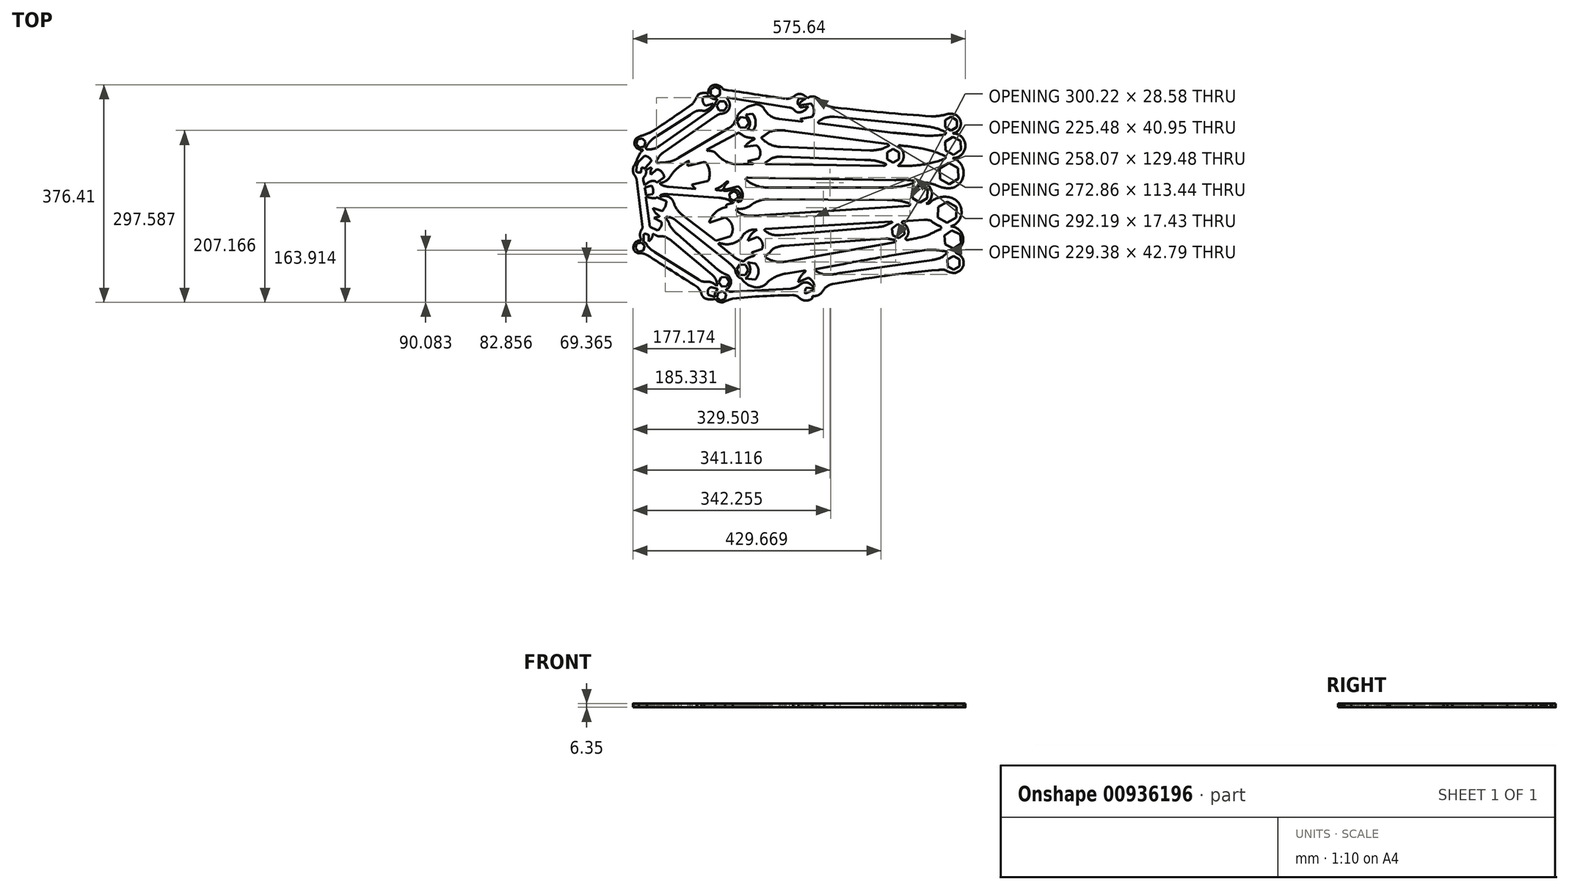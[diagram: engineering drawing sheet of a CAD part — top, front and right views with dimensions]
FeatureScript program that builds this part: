
annotation { "Feature Type Name" : "Feature", "Feature Type Description" : "" }
export const myFeature = defineFeature(function(context is Context, id is Id, definition is map)
    precondition{}
    {
        {
            var Q0;
            Q0=qCreatedBy(makeId("Top.planeOp"),FACE);
            var sketch = newSketch(context, id + "F0", { "sketchPlane" : qUnion([Q0])});
            skArc(sketch, "E0", {"start": v(-55.05, 260.44) * mm, "mid": v(-35.77, 286.45) * mm, "end": v(-55.34, 312.24) * mm});
            skArc(sketch, "E1", {"start": v(-55.34, 312.24) * mm, "mid": v(-32.71, 333.5) * mm, "end": v(-55.34, 354.78) * mm});
            skArc(sketch, "E2", {"start": v(-55.34, 354.78) * mm, "mid": v(-40.48, 371.7) * mm, "end": v(-55.34, 388.63) * mm});
            skArc(sketch, "E3", {"start": v(-58.23, 193.89) * mm, "mid": v(-39.5, 221.81) * mm, "end": v(-64.02, 244.82) * mm});
            skArc(sketch, "E4", {"start": v(-48.1, 151.93) * mm, "mid": v(-37.16, 176.78) * mm, "end": v(-58.23, 193.89) * mm});
            skArc(sketch, "E5", {"start": v(-50.13, 113.44) * mm, "mid": v(-35.84, 129.58) * mm, "end": v(-48.1, 147.3) * mm});
            skArc(sketch, "E6", {"start": v(-48.1, 151.93) * mm, "mid": v(-49.62, 149.62) * mm, "end": v(-48.1, 147.3) * mm});
            skArc(sketch, "E7", {"start": v(-67.06, 118.5) * mm, "mid": v(-59.11, 114.24) * mm, "end": v(-50.13, 113.44) * mm});
            skArc(sketch, "E8", {"start": v(-67.06, 118.5) * mm, "mid": v(-73.43, 118.66) * mm, "end": v(-79.8, 118.5) * mm});
            skArc(sketch, "E9", {"start": v(-79.8, 118.5) * mm, "mid": v(-171.14, 108.32) * mm, "end": v(-261.94, 94.05) * mm});
            skArc(sketch, "E10", {"start": v(-261.94, 94.05) * mm, "mid": v(-270.5, 91.02) * mm, "end": v(-277.56, 85.32) * mm});
            skArc(sketch, "E11", {"start": v(-297.54, 73.15) * mm, "mid": v(-285.53, 75.93) * mm, "end": v(-277.56, 85.32) * mm});
            skArc(sketch, "E12", {"start": v(-321.56, 71.59) * mm, "mid": v(-310, 65.3) * mm, "end": v(-297.54, 69.56) * mm});
            skArc(sketch, "E13", {"start": v(-321.56, 71.59) * mm, "mid": v(-326.02, 73.88) * mm, "end": v(-330.96, 74.77) * mm});
            skArc(sketch, "E14", {"start": v(-330.96, 74.77) * mm, "mid": v(-383.12, 73.1) * mm, "end": v(-435.13, 68.84) * mm});
            skArc(sketch, "E15", {"start": v(-435.13, 68.84) * mm, "mid": v(-442.05, 66.61) * mm, "end": v(-448.79, 63.89) * mm});
            skArc(sketch, "E16", {"start": v(-465.74, 68.84) * mm, "mid": v(-458.25, 62.97) * mm, "end": v(-448.79, 63.89) * mm});
            skArc(sketch, "E17", {"start": v(-484.84, 70.12) * mm, "mid": v(-475.44, 67.23) * mm, "end": v(-465.74, 68.84) * mm});
            skArc(sketch, "E18", {"start": v(-489.9, 78.95) * mm, "mid": v(-488.33, 73.99) * mm, "end": v(-484.84, 70.12) * mm});
            skArc(sketch, "E19", {"start": v(-489.9, 78.95) * mm, "mid": v(-493.3, 84.37) * mm, "end": v(-497.34, 89.32) * mm});
            skArc(sketch, "E20", {"start": v(-583.93, 144.4) * mm, "mid": v(-540.7, 116.75) * mm, "end": v(-497.34, 89.32) * mm});
            skArc(sketch, "E21", {"start": v(-583.93, 144.4) * mm, "mid": v(-590.67, 146.93) * mm, "end": v(-597.87, 147.3) * mm});
            skArc(sketch, "E22", {"start": v(-606.71, 161.55) * mm, "mid": v(-606, 152.12) * mm, "end": v(-597.87, 147.3) * mm});
            skArc(sketch, "E23", {"start": v(-594.42, 169.3) * mm, "mid": v(-601.98, 167.67) * mm, "end": v(-606.71, 161.55) * mm});
            skArc(sketch, "E24", {"start": v(-593.23, 187.82) * mm, "mid": v(-595.96, 179.21) * mm, "end": v(-593.23, 170.6) * mm});
            skArc(sketch, "E25", {"start": v(-593.23, 187.82) * mm, "mid": v(-592.2, 189.97) * mm, "end": v(-591.78, 192.3) * mm});
            skArc(sketch, "E26", {"start": v(-591.78, 192.3) * mm, "mid": v(-596.7, 233.52) * mm, "end": v(-601.66, 274.73) * mm});
            skArc(sketch, "E27", {"start": v(-601.66, 274.73) * mm, "mid": v(-602.84, 277.85) * mm, "end": v(-604.25, 280.88) * mm});
            skArc(sketch, "E28", {"start": v(-604.25, 301.71) * mm, "mid": v(-608.35, 291.3) * mm, "end": v(-604.25, 280.88) * mm});
            skArc(sketch, "E29", {"start": v(-590.37, 326.53) * mm, "mid": v(-597.45, 317.75) * mm, "end": v(-601.66, 307.28) * mm});
            skArc(sketch, "E30", {"start": v(-604.25, 333.1) * mm, "mid": v(-598.39, 327.55) * mm, "end": v(-590.37, 326.53) * mm});
            skArc(sketch, "E31", {"start": v(-600.43, 347.65) * mm, "mid": v(-605.16, 341.12) * mm, "end": v(-604.25, 333.1) * mm});
            skArc(sketch, "E32", {"start": v(-591.78, 351.27) * mm, "mid": v(-596.23, 349.75) * mm, "end": v(-600.43, 347.65) * mm});
            skArc(sketch, "E33", {"start": v(-591.78, 351.27) * mm, "mid": v(-583.33, 354.16) * mm, "end": v(-575.25, 358) * mm});
            skArc(sketch, "E34", {"start": v(-575.25, 358) * mm, "mid": v(-540.45, 381.34) * mm, "end": v(-505.94, 405.1) * mm});
            skArc(sketch, "E35", {"start": v(-505.94, 405.1) * mm, "mid": v(-500.06, 413.35) * mm, "end": v(-495.19, 422.24) * mm});
            skArc(sketch, "E36", {"start": v(-477.33, 423.44) * mm, "mid": v(-486.4, 424.91) * mm, "end": v(-495.19, 422.24) * mm});
            skArc(sketch, "E37", {"start": v(-468.58, 438.6) * mm, "mid": v(-476.1, 432.83) * mm, "end": v(-477.33, 423.44) * mm});
            skArc(sketch, "E38", {"start": v(-453.3, 432.68) * mm, "mid": v(-460.1, 437.83) * mm, "end": v(-468.58, 438.6) * mm});
            skArc(sketch, "E39", {"start": v(-453.3, 432.68) * mm, "mid": v(-451.18, 431.1) * mm, "end": v(-448.68, 430.22) * mm});
            skArc(sketch, "E40", {"start": v(-448.68, 430.22) * mm, "mid": v(-395.94, 422.55) * mm, "end": v(-343.2, 414.89) * mm});
            skArc(sketch, "E41", {"start": v(-343.2, 414.89) * mm, "mid": v(-335.76, 415.8) * mm, "end": v(-329.02, 419.08) * mm});
            skArc(sketch, "E42", {"start": v(-314.84, 422.24) * mm, "mid": v(-322.42, 422.86) * mm, "end": v(-329.02, 419.08) * mm});
            skArc(sketch, "E43", {"start": v(-307.75, 417.2) * mm, "mid": v(-311.06, 420.06) * mm, "end": v(-314.84, 422.24) * mm});
            skArc(sketch, "E44", {"start": v(-290.54, 416.91) * mm, "mid": v(-298.22, 418.8) * mm, "end": v(-305.73, 416.33) * mm});
            skArc(sketch, "E45", {"start": v(-284.64, 413.56) * mm, "mid": v(-287.52, 415.36) * mm, "end": v(-290.54, 416.91) * mm});
            skArc(sketch, "E46", {"start": v(-284.64, 413.56) * mm, "mid": v(-280.96, 408.46) * mm, "end": v(-275.63, 405.1) * mm});
            skArc(sketch, "E47", {"start": v(-275.63, 405.1) * mm, "mid": v(-267.42, 401.3) * mm, "end": v(-258.53, 399.62) * mm});
            skArc(sketch, "E48", {"start": v(-258.53, 399.62) * mm, "mid": v(-175.22, 391.15) * mm, "end": v(-91.74, 384.4) * mm});
            skArc(sketch, "E49", {"start": v(-91.74, 384.4) * mm, "mid": v(-79.83, 385.04) * mm, "end": v(-68.09, 387.15) * mm});
            skArc(sketch, "E50", {"start": v(-55.34, 388.63) * mm, "mid": v(-61.8, 388.7) * mm, "end": v(-68.09, 387.15) * mm});
            skArc(sketch, "E51", {"start": v(-83.4, 265.2) * mm, "mid": v(-69.62, 260.51) * mm, "end": v(-55.05, 260.44) * mm});
            skArc(sketch, "E52", {"start": v(-83.4, 265.2) * mm, "mid": v(-92.57, 267.9) * mm, "end": v(-101.93, 269.83) * mm});
            skArc(sketch, "E53", {"start": v(-90.64, 251.46) * mm, "mid": v(-94.28, 261.88) * mm, "end": v(-101.93, 269.83) * mm});
            skArc(sketch, "E54", {"start": v(-100.48, 233.08) * mm, "mid": v(-93.22, 241.02) * mm, "end": v(-90.64, 251.46) * mm});
            skArc(sketch, "E55", {"start": v(-64.02, 244.82) * mm, "mid": v(-81.43, 242.82) * mm, "end": v(-96, 233.08) * mm});
            skLineSegment(sketch, "E56", {"start": v(-297.54, 69.56) * mm, "end": v(-297.54, 73.15) * mm});
            skLineSegment(sketch, "E57", {"start": v(-594.42, 169.3) * mm, "end": v(-593.23, 170.6) * mm});
            skLineSegment(sketch, "E58", {"start": v(-604.25, 301.71) * mm, "end": v(-601.66, 307.28) * mm});
            skLineSegment(sketch, "E59", {"start": v(-305.73, 416.33) * mm, "end": v(-307.75, 417.2) * mm});
            skCircle(sketch, "E60.cCircle", {"center": v(-57.55, 371.7) * mm, "radius": 10.32 * mm, "construction": true});
            skLineSegment(sketch, "E60.0", {"start": v(-57.68, 359.8) * mm, "end": v(-67.93, 365.86) * mm});
            skLineSegment(sketch, "E60.1", {"start": v(-67.93, 365.86) * mm, "end": v(-67.8, 377.77) * mm});
            skLineSegment(sketch, "E60.2", {"start": v(-67.8, 377.77) * mm, "end": v(-57.43, 383.62) * mm});
            skLineSegment(sketch, "E60.3", {"start": v(-57.43, 383.62) * mm, "end": v(-47.17, 377.55) * mm});
            skLineSegment(sketch, "E60.4", {"start": v(-47.17, 377.55) * mm, "end": v(-47.3, 365.64) * mm});
            skLineSegment(sketch, "E60.5", {"start": v(-47.3, 365.64) * mm, "end": v(-57.68, 359.8) * mm});
            skPoint(sketch, "E60.0.midPoint", {"position": v(-62.8, 362.82) * mm});
            skCircle(sketch, "E61.cCircle", {"center": v(-54.02, 333.5) * mm, "radius": 13.49 * mm, "construction": true});
            skLineSegment(sketch, "E61.0", {"start": v(-53.4, 317.95) * mm, "end": v(-67.18, 325.18) * mm});
            skLineSegment(sketch, "E61.1", {"start": v(-67.18, 325.18) * mm, "end": v(-67.81, 340.74) * mm});
            skLineSegment(sketch, "E61.2", {"start": v(-67.81, 340.74) * mm, "end": v(-54.65, 349.07) * mm});
            skLineSegment(sketch, "E61.3", {"start": v(-54.65, 349.07) * mm, "end": v(-40.86, 341.83) * mm});
            skLineSegment(sketch, "E61.4", {"start": v(-40.86, 341.83) * mm, "end": v(-40.23, 326.27) * mm});
            skLineSegment(sketch, "E61.5", {"start": v(-40.23, 326.27) * mm, "end": v(-53.4, 317.95) * mm});
            skPoint(sketch, "E61.0.midPoint", {"position": v(-60.29, 321.56) * mm});
            skCircle(sketch, "E62.cCircle", {"center": v(-61.13, 285.32) * mm, "radius": 15.88 * mm, "construction": true});
            skLineSegment(sketch, "E62.0", {"start": v(-61.01, 267) * mm, "end": v(-76.95, 276.05) * mm});
            skLineSegment(sketch, "E62.1", {"start": v(-76.95, 276.05) * mm, "end": v(-77.07, 294.38) * mm});
            skLineSegment(sketch, "E62.2", {"start": v(-77.07, 294.38) * mm, "end": v(-61.26, 303.65) * mm});
            skLineSegment(sketch, "E62.3", {"start": v(-61.26, 303.65) * mm, "end": v(-45.32, 294.6) * mm});
            skLineSegment(sketch, "E62.4", {"start": v(-45.32, 294.6) * mm, "end": v(-45.2, 276.26) * mm});
            skLineSegment(sketch, "E62.5", {"start": v(-45.2, 276.26) * mm, "end": v(-61.01, 267) * mm});
            skPoint(sketch, "E62.0.midPoint", {"position": v(-68.98, 271.52) * mm});
            skCircle(sketch, "E63.cCircle", {"center": v(-111.31, 250.03) * mm, "radius": 12.7 * mm, "construction": true});
            skLineSegment(sketch, "E63.0", {"start": v(-111.59, 235.37) * mm, "end": v(-124.15, 242.94) * mm});
            skLineSegment(sketch, "E63.1", {"start": v(-124.15, 242.94) * mm, "end": v(-123.87, 257.6) * mm});
            skLineSegment(sketch, "E63.2", {"start": v(-123.87, 257.6) * mm, "end": v(-111.03, 264.7) * mm});
            skLineSegment(sketch, "E63.3", {"start": v(-111.03, 264.7) * mm, "end": v(-98.47, 257.12) * mm});
            skLineSegment(sketch, "E63.4", {"start": v(-98.47, 257.12) * mm, "end": v(-98.75, 242.46) * mm});
            skLineSegment(sketch, "E63.5", {"start": v(-98.75, 242.46) * mm, "end": v(-111.59, 235.37) * mm});
            skPoint(sketch, "E63.0.midPoint", {"position": v(-117.87, 239.16) * mm});
            skCircle(sketch, "E64.cCircle", {"center": v(-64.33, 218.26) * mm, "radius": 15.88 * mm, "construction": true});
            skLineSegment(sketch, "E64.0", {"start": v(-64.51, 199.93) * mm, "end": v(-80.3, 209.26) * mm});
            skLineSegment(sketch, "E64.1", {"start": v(-80.3, 209.26) * mm, "end": v(-80.1, 227.59) * mm});
            skLineSegment(sketch, "E64.2", {"start": v(-80.1, 227.59) * mm, "end": v(-64.14, 236.6) * mm});
            skLineSegment(sketch, "E64.3", {"start": v(-64.14, 236.6) * mm, "end": v(-48.36, 227.27) * mm});
            skLineSegment(sketch, "E64.4", {"start": v(-48.36, 227.27) * mm, "end": v(-48.55, 208.94) * mm});
            skLineSegment(sketch, "E64.5", {"start": v(-48.55, 208.94) * mm, "end": v(-64.51, 199.93) * mm});
            skPoint(sketch, "E64.0.midPoint", {"position": v(-72.4, 204.6) * mm});
            skCircle(sketch, "E65.cCircle", {"center": v(-149.16, 185.48) * mm, "radius": 10.32 * mm, "construction": true});
            skLineSegment(sketch, "E65.0", {"start": v(-147.9, 173.63) * mm, "end": v(-158.79, 178.46) * mm});
            skLineSegment(sketch, "E65.1", {"start": v(-158.79, 178.46) * mm, "end": v(-160.05, 190.3) * mm});
            skLineSegment(sketch, "E65.2", {"start": v(-160.05, 190.3) * mm, "end": v(-150.42, 197.33) * mm});
            skLineSegment(sketch, "E65.3", {"start": v(-150.42, 197.33) * mm, "end": v(-139.53, 192.5) * mm});
            skLineSegment(sketch, "E65.4", {"start": v(-139.53, 192.5) * mm, "end": v(-138.27, 180.65) * mm});
            skLineSegment(sketch, "E65.5", {"start": v(-138.27, 180.65) * mm, "end": v(-147.9, 173.63) * mm});
            skPoint(sketch, "E65.0.midPoint", {"position": v(-153.34, 176.04) * mm});
            skCircle(sketch, "E66.cCircle", {"center": v(-54.8, 171.29) * mm, "radius": 13.49 * mm, "construction": true});
            skLineSegment(sketch, "E66.0", {"start": v(-53.58, 155.76) * mm, "end": v(-67.64, 162.47) * mm});
            skLineSegment(sketch, "E66.1", {"start": v(-67.64, 162.47) * mm, "end": v(-68.86, 178) * mm});
            skLineSegment(sketch, "E66.2", {"start": v(-68.86, 178) * mm, "end": v(-56.02, 186.81) * mm});
            skLineSegment(sketch, "E66.3", {"start": v(-56.02, 186.81) * mm, "end": v(-41.97, 180.11) * mm});
            skLineSegment(sketch, "E66.4", {"start": v(-41.97, 180.11) * mm, "end": v(-40.74, 164.58) * mm});
            skLineSegment(sketch, "E66.5", {"start": v(-40.74, 164.58) * mm, "end": v(-53.58, 155.76) * mm});
            skPoint(sketch, "E66.0.midPoint", {"position": v(-60.6, 159.11) * mm});
            skCircle(sketch, "E67.cCircle", {"center": v(-53.27, 130.62) * mm, "radius": 10.32 * mm, "construction": true});
            skLineSegment(sketch, "E67.0", {"start": v(-42.86, 124.82) * mm, "end": v(-53.1, 118.7) * mm});
            skLineSegment(sketch, "E67.1", {"start": v(-53.1, 118.7) * mm, "end": v(-63.5, 124.51) * mm});
            skLineSegment(sketch, "E67.2", {"start": v(-63.5, 124.51) * mm, "end": v(-63.67, 136.43) * mm});
            skLineSegment(sketch, "E67.3", {"start": v(-63.67, 136.43) * mm, "end": v(-53.44, 142.53) * mm});
            skLineSegment(sketch, "E67.4", {"start": v(-53.44, 142.53) * mm, "end": v(-43.04, 136.73) * mm});
            skLineSegment(sketch, "E67.5", {"start": v(-43.04, 136.73) * mm, "end": v(-42.86, 124.82) * mm});
            skPoint(sketch, "E67.0.midPoint", {"position": v(-47.98, 121.76) * mm});
            skCircle(sketch, "E68.cCircle", {"center": v(-157.91, 316.16) * mm, "radius": 10.32 * mm, "construction": true});
            skLineSegment(sketch, "E68.0", {"start": v(-168.23, 310.2) * mm, "end": v(-168.23, 322.12) * mm});
            skLineSegment(sketch, "E68.1", {"start": v(-168.23, 322.12) * mm, "end": v(-157.91, 328.08) * mm});
            skLineSegment(sketch, "E68.2", {"start": v(-157.91, 328.08) * mm, "end": v(-147.6, 322.12) * mm});
            skLineSegment(sketch, "E68.3", {"start": v(-147.6, 322.12) * mm, "end": v(-147.6, 310.2) * mm});
            skLineSegment(sketch, "E68.4", {"start": v(-147.6, 310.2) * mm, "end": v(-157.91, 304.25) * mm});
            skLineSegment(sketch, "E68.5", {"start": v(-157.91, 304.25) * mm, "end": v(-168.23, 310.2) * mm});
            skPoint(sketch, "E68.0.midPoint", {"position": v(-168.23, 316.16) * mm});
            skArc(sketch, "E69", {"start": v(-67.1, 356.86) * mm, "mid": v(-81.33, 363.08) * mm, "end": v(-96.49, 366.5) * mm});
            skArc(sketch, "E70", {"start": v(-117.16, 352.27) * mm, "mid": v(-92.55, 350.73) * mm, "end": v(-68, 353.19) * mm});
            skArc(sketch, "E71", {"start": v(-68.7, 315.98) * mm, "mid": v(-88.6, 323.76) * mm, "end": v(-109.35, 328.84) * mm});
            skArc(sketch, "E72", {"start": v(-111.65, 300.13) * mm, "mid": v(-89.98, 304.15) * mm, "end": v(-68.93, 310.7) * mm});
            skArc(sketch, "E73", {"start": v(-68, 353.19) * mm, "mid": v(-66.78, 354.83) * mm, "end": v(-67.1, 356.86) * mm});
            skArc(sketch, "E74", {"start": v(-68.93, 310.7) * mm, "mid": v(-66.96, 313.26) * mm, "end": v(-68.7, 315.98) * mm});
            skLineSegment(sketch, "E75", {"start": v(-96, 233.08) * mm, "end": v(-100.48, 233.08) * mm});
            skArc(sketch, "E76", {"start": v(-93.08, 204.03) * mm, "mid": v(-84.94, 198.29) * mm, "end": v(-76, 193.9) * mm});
            skArc(sketch, "E77", {"start": v(-93.08, 204.03) * mm, "mid": v(-98.82, 205.1) * mm, "end": v(-104.65, 205.33) * mm});
            skArc(sketch, "E78", {"start": v(-74.56, 189.7) * mm, "mid": v(-86.96, 183.92) * mm, "end": v(-99.15, 177.7) * mm});
            skArc(sketch, "E79", {"start": v(-134.17, 170.17) * mm, "mid": v(-116.6, 173.63) * mm, "end": v(-99.15, 177.7) * mm});
            skArc(sketch, "E80", {"start": v(-136.05, 173.2) * mm, "mid": v(-131.94, 188.07) * mm, "end": v(-142.56, 199.25) * mm});
            skLineSegment(sketch, "E81", {"start": v(-104.65, 205.33) * mm, "end": v(-141.4, 203.01) * mm});
            skArc(sketch, "E82", {"start": v(-141.4, 203.01) * mm, "mid": v(-142.3, 201.23) * mm, "end": v(-142.56, 199.25) * mm});
            skArc(sketch, "E83", {"start": v(-136.05, 173.2) * mm, "mid": v(-135.8, 171.26) * mm, "end": v(-134.17, 170.17) * mm});
            skArc(sketch, "E84", {"start": v(-74.56, 189.7) * mm, "mid": v(-74.67, 192.01) * mm, "end": v(-76, 193.9) * mm});
            skArc(sketch, "E85", {"start": v(-66, 150.5) * mm, "mid": v(-72.3, 151.46) * mm, "end": v(-78.62, 152.33) * mm});
            skArc(sketch, "E86", {"start": v(-78.62, 152.33) * mm, "mid": v(-89.14, 153.18) * mm, "end": v(-99.7, 152.96) * mm});
            skArc(sketch, "E87", {"start": v(-99.7, 152.96) * mm, "mid": v(-132, 148.18) * mm, "end": v(-164.2, 142.78) * mm});
            skArc(sketch, "E88", {"start": v(-164.2, 142.78) * mm, "mid": v(-202.8, 136.25) * mm, "end": v(-241.31, 129.29) * mm});
            skLineSegment(sketch, "E89", {"start": v(-241.31, 129.29) * mm, "end": v(-293.37, 119.57) * mm});
            skArc(sketch, "E90", {"start": v(-291.22, 116.51) * mm, "mid": v(-285, 113.2) * mm, "end": v(-278.35, 110.89) * mm});
            skArc(sketch, "E91", {"start": v(-278.35, 110.89) * mm, "mid": v(-264, 110.66) * mm, "end": v(-249.87, 113.18) * mm});
            skLineSegment(sketch, "E92", {"start": v(-249.87, 113.18) * mm, "end": v(-90.32, 135.62) * mm});
            skArc(sketch, "E93", {"start": v(-90.32, 135.62) * mm, "mid": v(-80.84, 137.71) * mm, "end": v(-71.8, 141.26) * mm});
            skArc(sketch, "E94", {"start": v(-64, 147.91) * mm, "mid": v(-68.09, 144.8) * mm, "end": v(-71.8, 141.26) * mm});
            skArc(sketch, "E95", {"start": v(-64, 147.91) * mm, "mid": v(-64.5, 149.58) * mm, "end": v(-66, 150.5) * mm});
            skArc(sketch, "E96", {"start": v(-293.37, 119.57) * mm, "mid": v(-292.66, 117.78) * mm, "end": v(-291.22, 116.51) * mm});
            skArc(sketch, "E97", {"start": v(-148.24, 298.5) * mm, "mid": v(-129.91, 298.62) * mm, "end": v(-111.65, 300.13) * mm});
            skArc(sketch, "E98", {"start": v(-148.59, 300.13) * mm, "mid": v(-139.57, 315.6) * mm, "end": v(-147.9, 331.45) * mm});
            skArc(sketch, "E99", {"start": v(-109.35, 328.84) * mm, "mid": v(-128.57, 331.94) * mm, "end": v(-147.9, 334.2) * mm});
            skArc(sketch, "E100", {"start": v(-147.9, 334.2) * mm, "mid": v(-148.37, 332.83) * mm, "end": v(-147.9, 331.45) * mm});
            skArc(sketch, "E101", {"start": v(-148.59, 300.13) * mm, "mid": v(-149.15, 299.16) * mm, "end": v(-148.24, 298.5) * mm});
            skArc(sketch, "E102", {"start": v(-96.49, 366.5) * mm, "mid": v(-111.46, 368.54) * mm, "end": v(-126.48, 370.2) * mm});
            skArc(sketch, "E103", {"start": v(-117.16, 352.27) * mm, "mid": v(-137.44, 354.16) * mm, "end": v(-157.73, 356.01) * mm});
            skArc(sketch, "E104", {"start": v(-259.78, 383.5) * mm, "mid": v(-274.29, 382.2) * mm, "end": v(-287.12, 375.3) * mm});
            skLineSegment(sketch, "E105", {"start": v(-259.78, 383.5) * mm, "end": v(-126.48, 370.2) * mm});
            skLineSegment(sketch, "E106", {"start": v(-157.73, 356.01) * mm, "end": v(-285.48, 372.02) * mm});
            skArc(sketch, "E107", {"start": v(-287.12, 375.3) * mm, "mid": v(-287.18, 373.22) * mm, "end": v(-285.48, 372.02) * mm});
            skArc(sketch, "E108", {"start": v(-164.93, 333.3) * mm, "mid": v(-171.01, 330.8) * mm, "end": v(-176.93, 327.95) * mm});
            skArc(sketch, "E109", {"start": v(-197.62, 325.06) * mm, "mid": v(-187.22, 326.07) * mm, "end": v(-176.93, 327.95) * mm});
            skArc(sketch, "E110", {"start": v(-169.56, 301.18) * mm, "mid": v(-179.82, 305.22) * mm, "end": v(-190.53, 307.84) * mm});
            skArc(sketch, "E111", {"start": v(-190.53, 307.84) * mm, "mid": v(-198.87, 308.58) * mm, "end": v(-207.25, 308.49) * mm});
            skArc(sketch, "E112", {"start": v(-385.9, 347.4) * mm, "mid": v(-378.66, 352.33) * mm, "end": v(-371.68, 357.6) * mm});
            skArc(sketch, "E113", {"start": v(-344.33, 359.8) * mm, "mid": v(-358.13, 360.3) * mm, "end": v(-371.68, 357.6) * mm});
            skArc(sketch, "E114", {"start": v(-383.34, 344.12) * mm, "mid": v(-369.1, 335.15) * mm, "end": v(-352.72, 331.36) * mm});
            skLineSegment(sketch, "E115", {"start": v(-344.33, 359.8) * mm, "end": v(-168.48, 336.6) * mm});
            skLineSegment(sketch, "E116", {"start": v(-197.62, 325.06) * mm, "end": v(-352.72, 331.36) * mm});
            skArc(sketch, "E117", {"start": v(-164.93, 333.3) * mm, "mid": v(-166.18, 335.52) * mm, "end": v(-168.48, 336.6) * mm});
            skArc(sketch, "E118", {"start": v(-385.9, 347.4) * mm, "mid": v(-384.7, 345.7) * mm, "end": v(-383.34, 344.12) * mm});
            skArc(sketch, "E119", {"start": v(-379.38, 303.88) * mm, "mid": v(-374.36, 307.19) * mm, "end": v(-369.7, 310.97) * mm});
            skArc(sketch, "E120", {"start": v(-349.87, 314.3) * mm, "mid": v(-360, 314) * mm, "end": v(-369.7, 310.97) * mm});
            skLineSegment(sketch, "E121", {"start": v(-349.87, 314.3) * mm, "end": v(-207.25, 308.49) * mm});
            skLineSegment(sketch, "E122", {"start": v(-174.14, 298.88) * mm, "end": v(-377.13, 301.63) * mm});
            skArc(sketch, "E123", {"start": v(-379.38, 303.88) * mm, "mid": v(-378.71, 302.3) * mm, "end": v(-377.13, 301.63) * mm});
            skArc(sketch, "E124", {"start": v(-174.14, 298.88) * mm, "mid": v(-171.56, 299.47) * mm, "end": v(-169.56, 301.18) * mm});
            skArc(sketch, "E125", {"start": v(-121.66, 272.58) * mm, "mid": v(-138.57, 274.43) * mm, "end": v(-155.57, 273.85) * mm});
            skArc(sketch, "E126", {"start": v(-166.32, 260.9) * mm, "mid": v(-144, 263.1) * mm, "end": v(-122.4, 269.11) * mm});
            skArc(sketch, "E127", {"start": v(-413.33, 274.76) * mm, "mid": v(-391.7, 263.47) * mm, "end": v(-367.4, 261.27) * mm});
            skLineSegment(sketch, "E128", {"start": v(-166.32, 260.9) * mm, "end": v(-367.4, 261.27) * mm});
            skLineSegment(sketch, "E129", {"start": v(-155.57, 273.85) * mm, "end": v(-409.58, 278.34) * mm});
            skArc(sketch, "E130", {"start": v(-409.58, 278.34) * mm, "mid": v(-412.19, 277.32) * mm, "end": v(-413.33, 274.76) * mm});
            skArc(sketch, "E131", {"start": v(-122.4, 269.11) * mm, "mid": v(-121.19, 270.67) * mm, "end": v(-121.66, 272.58) * mm});
            skArc(sketch, "E132", {"start": v(-143.46, 237.66) * mm, "mid": v(-136.26, 235.54) * mm, "end": v(-129, 233.64) * mm});
            skArc(sketch, "E133", {"start": v(-143.46, 237.66) * mm, "mid": v(-150.45, 238.66) * mm, "end": v(-157.47, 239.38) * mm});
            skArc(sketch, "E134", {"start": v(-157.47, 239.38) * mm, "mid": v(-162.74, 239.57) * mm, "end": v(-168.01, 239.38) * mm});
            skArc(sketch, "E135", {"start": v(-427.88, 224.36) * mm, "mid": v(-415.13, 225) * mm, "end": v(-403.76, 230.79) * mm});
            skArc(sketch, "E136", {"start": v(-372.99, 240.67) * mm, "mid": v(-389.25, 238.46) * mm, "end": v(-403.76, 230.79) * mm});
            skArc(sketch, "E137", {"start": v(-428.8, 220.8) * mm, "mid": v(-415.65, 213.52) * mm, "end": v(-400.66, 212.42) * mm});
            skLineSegment(sketch, "E138", {"start": v(-372.99, 240.67) * mm, "end": v(-168.01, 239.38) * mm});
            skLineSegment(sketch, "E139", {"start": v(-129.52, 229.7) * mm, "end": v(-400.66, 212.42) * mm});
            skArc(sketch, "E140", {"start": v(-129.52, 229.7) * mm, "mid": v(-128.78, 231.6) * mm, "end": v(-129, 233.64) * mm});
            skArc(sketch, "E141", {"start": v(-427.88, 224.36) * mm, "mid": v(-428.85, 222.71) * mm, "end": v(-428.8, 220.8) * mm});
            skArc(sketch, "E142", {"start": v(-159.24, 200.42) * mm, "mid": v(-165.55, 197.98) * mm, "end": v(-171.68, 195.07) * mm});
            skArc(sketch, "E143", {"start": v(-184.27, 192.76) * mm, "mid": v(-177.88, 193.39) * mm, "end": v(-171.68, 195.07) * mm});
            skArc(sketch, "E144", {"start": v(-380.9, 187.11) * mm, "mid": v(-367.8, 180) * mm, "end": v(-352.97, 178.72) * mm});
            skLineSegment(sketch, "E145", {"start": v(-378.49, 189.12) * mm, "end": v(-161.45, 202.22) * mm});
            skLineSegment(sketch, "E146", {"start": v(-184.27, 192.76) * mm, "end": v(-352.97, 178.72) * mm});
            skArc(sketch, "E147", {"start": v(-378.49, 189.12) * mm, "mid": v(-380.02, 188.52) * mm, "end": v(-380.9, 187.11) * mm});
            skArc(sketch, "E148", {"start": v(-159.24, 200.42) * mm, "mid": v(-160, 201.75) * mm, "end": v(-161.45, 202.22) * mm});
            skArc(sketch, "E149", {"start": v(-153.36, 169.7) * mm, "mid": v(-161.9, 171.67) * mm, "end": v(-170.57, 173.02) * mm});
            skArc(sketch, "E150", {"start": v(-378.49, 143.65) * mm, "mid": v(-372.4, 147.7) * mm, "end": v(-367.7, 153.31) * mm});
            skArc(sketch, "E151", {"start": v(-346.38, 160.24) * mm, "mid": v(-357.55, 158.34) * mm, "end": v(-367.7, 153.31) * mm});
            skArc(sketch, "E152", {"start": v(-377, 139.28) * mm, "mid": v(-360.77, 132.8) * mm, "end": v(-343.28, 133.08) * mm});
            skLineSegment(sketch, "E153", {"start": v(-346.38, 160.24) * mm, "end": v(-170.57, 173.02) * mm});
            skLineSegment(sketch, "E154", {"start": v(-154.33, 166.83) * mm, "end": v(-343.28, 133.08) * mm});
            skArc(sketch, "E155", {"start": v(-378.49, 143.65) * mm, "mid": v(-378.67, 141.15) * mm, "end": v(-377, 139.28) * mm});
            skArc(sketch, "E156", {"start": v(-154.33, 166.83) * mm, "mid": v(-153.63, 168.2) * mm, "end": v(-153.36, 169.7) * mm});
            skArc(sketch, "E157", {"start": v(-464.33, 320.3) * mm, "mid": v(-449.46, 307.64) * mm, "end": v(-430.91, 301.53) * mm});
            skArc(sketch, "E158", {"start": v(-464.33, 320.3) * mm, "mid": v(-470.36, 323.84) * mm, "end": v(-477.35, 324.27) * mm});
            skArc(sketch, "E159", {"start": v(-442.67, 270.47) * mm, "mid": v(-448.36, 265.37) * mm, "end": v(-451.25, 258.3) * mm});
            skArc(sketch, "E160", {"start": v(-465.82, 258.07) * mm, "mid": v(-455.25, 263.36) * mm, "end": v(-446.14, 270.9) * mm});
            skArc(sketch, "E161", {"start": v(-463.43, 256.77) * mm, "mid": v(-458.11, 256.36) * mm, "end": v(-452.78, 256.44) * mm});
            skArc(sketch, "E162", {"start": v(-390.76, 311.47) * mm, "mid": v(-387.83, 323.66) * mm, "end": v(-394.6, 334.21) * mm});
            skArc(sketch, "E163", {"start": v(-477.74, 272.85) * mm, "mid": v(-475.73, 290.08) * mm, "end": v(-483.5, 305.58) * mm});
            skArc(sketch, "E164", {"start": v(-399.83, 360.48) * mm, "mid": v(-395.84, 374.69) * mm, "end": v(-400.94, 388.53) * mm});
            skArc(sketch, "E165", {"start": v(-410.2, 361.29) * mm, "mid": v(-405.58, 372.67) * mm, "end": v(-410.65, 383.87) * mm});
            skArc(sketch, "E166", {"start": v(-297.8, 383.87) * mm, "mid": v(-294.81, 395.55) * mm, "end": v(-300.32, 406.27) * mm});
            skArc(sketch, "E167", {"start": v(-320.92, 415.03) * mm, "mid": v(-322.88, 410.4) * mm, "end": v(-322.56, 405.37) * mm});
            skArc(sketch, "E168", {"start": v(-310.37, 414.28) * mm, "mid": v(-315.84, 410.58) * mm, "end": v(-320.3, 405.72) * mm});
            skArc(sketch, "E169", {"start": v(-321.13, 391.08) * mm, "mid": v(-311.6, 394.2) * mm, "end": v(-304.9, 401.7) * mm});
            skArc(sketch, "E170", {"start": v(-328.29, 394.77) * mm, "mid": v(-325.16, 392.04) * mm, "end": v(-321.13, 391.08) * mm});
            skArc(sketch, "E171", {"start": v(-328.29, 394.77) * mm, "mid": v(-332.63, 398.12) * mm, "end": v(-337.87, 399.77) * mm});
            skArc(sketch, "E172", {"start": v(-317.87, 380) * mm, "mid": v(-316.61, 377.9) * mm, "end": v(-314.55, 376.58) * mm});
            skArc(sketch, "E173", {"start": v(-381.79, 398.44) * mm, "mid": v(-370.9, 385.69) * mm, "end": v(-355.15, 379.96) * mm});
            skArc(sketch, "E174", {"start": v(-381.79, 398.44) * mm, "mid": v(-387.48, 403.29) * mm, "end": v(-394.72, 405.18) * mm});
            skArc(sketch, "E175", {"start": v(-394.72, 405.18) * mm, "mid": v(-412.47, 399.13) * mm, "end": v(-426.8, 387.02) * mm});
            skArc(sketch, "E176", {"start": v(-426.69, 383.1) * mm, "mid": v(-430.77, 377.74) * mm, "end": v(-433.53, 371.58) * mm});
            skArc(sketch, "E177", {"start": v(-442.34, 363.76) * mm, "mid": v(-437.59, 367.28) * mm, "end": v(-433.53, 371.58) * mm});
            skArc(sketch, "E178", {"start": v(-424.51, 356.36) * mm, "mid": v(-412.5, 348.92) * mm, "end": v(-398.53, 346.8) * mm});
            skArc(sketch, "E179", {"start": v(-398.96, 343.97) * mm, "mid": v(-407.8, 338.73) * mm, "end": v(-414.94, 331.36) * mm});
            skArc(sketch, "E180", {"start": v(-409.18, 306.7) * mm, "mid": v(-405.17, 304.07) * mm, "end": v(-400.48, 303.1) * mm});
            skArc(sketch, "E181", {"start": v(-525.18, 299.5) * mm, "mid": v(-534.95, 291.41) * mm, "end": v(-542.8, 281.46) * mm});
            skArc(sketch, "E182", {"start": v(-558.54, 304.45) * mm, "mid": v(-543.34, 306.2) * mm, "end": v(-529.32, 312.33) * mm});
            skArc(sketch, "E183", {"start": v(-565.97, 303.33) * mm, "mid": v(-562.25, 303.85) * mm, "end": v(-558.54, 304.45) * mm});
            skArc(sketch, "E184", {"start": v(-555.87, 321.7) * mm, "mid": v(-563.14, 314.61) * mm, "end": v(-567.6, 305.49) * mm});
            skArc(sketch, "E185", {"start": v(-575.63, 294.3) * mm, "mid": v(-577.75, 289.09) * mm, "end": v(-577, 283.51) * mm});
            skArc(sketch, "E186", {"start": v(-585.81, 291.62) * mm, "mid": v(-581.93, 293.38) * mm, "end": v(-578.13, 295.33) * mm});
            skArc(sketch, "E187", {"start": v(-589.43, 278.76) * mm, "mid": v(-585.82, 284.68) * mm, "end": v(-585.81, 291.62) * mm});
            skArc(sketch, "E188", {"start": v(-589.43, 278.76) * mm, "mid": v(-590.39, 275.9) * mm, "end": v(-590.3, 272.9) * mm});
            skArc(sketch, "E189", {"start": v(-554.23, 278.76) * mm, "mid": v(-557.95, 288.02) * mm, "end": v(-566.74, 292.74) * mm});
            skArc(sketch, "E190", {"start": v(-561.22, 269.1) * mm, "mid": v(-552.95, 271.45) * mm, "end": v(-546.2, 276.78) * mm});
            skArc(sketch, "E191", {"start": v(-546.2, 276.78) * mm, "mid": v(-544.34, 279) * mm, "end": v(-542.8, 281.46) * mm});
            skArc(sketch, "E192", {"start": v(-574.04, 272.81) * mm, "mid": v(-581.67, 270.12) * mm, "end": v(-587.76, 264.79) * mm});
            skArc(sketch, "E193", {"start": v(-566.45, 269.88) * mm, "mid": v(-569.94, 272.12) * mm, "end": v(-574.04, 272.81) * mm});
            skArc(sketch, "E194", {"start": v(-560.32, 266.34) * mm, "mid": v(-553.43, 263.7) * mm, "end": v(-546.2, 262.2) * mm});
            skArc(sketch, "E195", {"start": v(-574.04, 249.86) * mm, "mid": v(-573.2, 257.44) * mm, "end": v(-575.77, 264.61) * mm});
            skArc(sketch, "E196", {"start": v(-584.4, 245.54) * mm, "mid": v(-578.22, 243.37) * mm, "end": v(-571.7, 242.7) * mm});
            skArc(sketch, "E197", {"start": v(-571.7, 242.7) * mm, "mid": v(-569.03, 242.9) * mm, "end": v(-566.62, 244.08) * mm});
            skArc(sketch, "E198", {"start": v(-543.67, 243.64) * mm, "mid": v(-551.51, 246.47) * mm, "end": v(-559.8, 245.54) * mm});
            skArc(sketch, "E199", {"start": v(-536.07, 230.1) * mm, "mid": v(-538.8, 237.47) * mm, "end": v(-543.67, 243.64) * mm});
            skArc(sketch, "E200", {"start": v(-547.98, 249.86) * mm, "mid": v(-554.69, 249.6) * mm, "end": v(-561.1, 247.61) * mm});
            skArc(sketch, "E201", {"start": v(-557.82, 220.26) * mm, "mid": v(-552.32, 228.25) * mm, "end": v(-550.48, 237.78) * mm});
            skArc(sketch, "E202", {"start": v(-573.26, 225.35) * mm, "mid": v(-569.33, 217.61) * mm, "end": v(-562.74, 211.98) * mm});
            skArc(sketch, "E203", {"start": v(-563.43, 210.25) * mm, "mid": v(-567.69, 209.77) * mm, "end": v(-571.7, 208.27) * mm});
            skArc(sketch, "E204", {"start": v(-537.2, 206.8) * mm, "mid": v(-543.77, 209.44) * mm, "end": v(-550.83, 210) * mm});
            skArc(sketch, "E205", {"start": v(-544.87, 196.01) * mm, "mid": v(-547.26, 202.65) * mm, "end": v(-552.04, 207.83) * mm});
            skArc(sketch, "E206", {"start": v(-565.58, 187.04) * mm, "mid": v(-559.78, 193.18) * mm, "end": v(-558.54, 201.54) * mm});
            skArc(sketch, "E207", {"start": v(-544.87, 196.01) * mm, "mid": v(-538.6, 187.77) * mm, "end": v(-531.5, 180.22) * mm});
            skArc(sketch, "E208", {"start": v(-571.7, 180.65) * mm, "mid": v(-565.6, 177.13) * mm, "end": v(-558.54, 176.94) * mm});
            skArc(sketch, "E209", {"start": v(-551.7, 175.56) * mm, "mid": v(-555.1, 176.35) * mm, "end": v(-558.54, 176.94) * mm});
            skArc(sketch, "E210", {"start": v(-541, 168.75) * mm, "mid": v(-546.27, 172.26) * mm, "end": v(-551.7, 175.56) * mm});
            skArc(sketch, "E211", {"start": v(-581.12, 167.88) * mm, "mid": v(-575.9, 172.94) * mm, "end": v(-574.04, 179.96) * mm});
            skArc(sketch, "E212", {"start": v(-580.86, 178.5) * mm, "mid": v(-584.87, 180.66) * mm, "end": v(-589.43, 180.48) * mm});
            skArc(sketch, "E213", {"start": v(-582.44, 159.26) * mm, "mid": v(-585.37, 163.8) * mm, "end": v(-589.43, 167.34) * mm});
            skArc(sketch, "E214", {"start": v(-582.44, 159.26) * mm, "mid": v(-576.84, 153.87) * mm, "end": v(-570.39, 149.53) * mm});
            skArc(sketch, "E215", {"start": v(-536.07, 230.1) * mm, "mid": v(-529.72, 220.48) * mm, "end": v(-521.4, 212.51) * mm});
            skArc(sketch, "E216", {"start": v(-584.16, 327.25) * mm, "mid": v(-572.22, 328.21) * mm, "end": v(-561.55, 333.63) * mm});
            skArc(sketch, "E217", {"start": v(-566.9, 349.85) * mm, "mid": v(-577.65, 341.94) * mm, "end": v(-585.37, 331.04) * mm});
            skArc(sketch, "E218", {"start": v(-576.12, 306.7) * mm, "mid": v(-580.82, 313.4) * mm, "end": v(-588.63, 315.86) * mm});
            skArc(sketch, "E219", {"start": v(-602.55, 288.95) * mm, "mid": v(-598.67, 287.08) * mm, "end": v(-594.4, 287.64) * mm});
            skArc(sketch, "E220", {"start": v(-445.4, 227.27) * mm, "mid": v(-464.8, 218.57) * mm, "end": v(-475.94, 200.43) * mm});
            skArc(sketch, "E221", {"start": v(-439.09, 176.94) * mm, "mid": v(-436.59, 195.5) * mm, "end": v(-449.23, 209.33) * mm});
            skArc(sketch, "E222", {"start": v(-421.56, 237.4) * mm, "mid": v(-418.56, 251.19) * mm, "end": v(-426.21, 263.02) * mm});
            skArc(sketch, "E223", {"start": v(-484.84, 393.65) * mm, "mid": v(-475.5, 398.33) * mm, "end": v(-469.09, 406.57) * mm});
            skArc(sketch, "E224", {"start": v(-484.84, 393.65) * mm, "mid": v(-491.48, 394.39) * mm, "end": v(-498.13, 393.65) * mm});
            skArc(sketch, "E225", {"start": v(-498.13, 393.65) * mm, "mid": v(-503.9, 390.67) * mm, "end": v(-509.36, 387.12) * mm});
            skArc(sketch, "E226", {"start": v(-486.76, 417.26) * mm, "mid": v(-487.08, 409.4) * mm, "end": v(-482.51, 403.01) * mm});
            skArc(sketch, "E227", {"start": v(-447.58, 391.1) * mm, "mid": v(-440.58, 402.22) * mm, "end": v(-444.84, 414.66) * mm});
            skArc(sketch, "E228", {"start": v(-585.37, 331.04) * mm, "mid": v(-585.53, 328.9) * mm, "end": v(-584.16, 327.25) * mm});
            skArc(sketch, "E229", {"start": v(-567.6, 305.49) * mm, "mid": v(-566.96, 304.28) * mm, "end": v(-565.97, 303.33) * mm});
            skArc(sketch, "E230", {"start": v(-575.63, 294.3) * mm, "mid": v(-576.77, 295.08) * mm, "end": v(-578.13, 295.33) * mm});
            skArc(sketch, "E231", {"start": v(-561.22, 269.1) * mm, "mid": v(-560.8, 267.7) * mm, "end": v(-560.32, 266.34) * mm});
            skArc(sketch, "E232", {"start": v(-561.1, 247.61) * mm, "mid": v(-560.85, 246.33) * mm, "end": v(-559.8, 245.54) * mm});
            skArc(sketch, "E233", {"start": v(-563.43, 210.25) * mm, "mid": v(-562.64, 210.94) * mm, "end": v(-562.74, 211.98) * mm});
            skArc(sketch, "E234", {"start": v(-550.83, 210) * mm, "mid": v(-551.79, 209.11) * mm, "end": v(-552.04, 207.83) * mm});
            skArc(sketch, "E235", {"start": v(-571.7, 180.65) * mm, "mid": v(-572.93, 180.5) * mm, "end": v(-574.04, 179.96) * mm});
            skArc(sketch, "E236", {"start": v(-452.78, 256.44) * mm, "mid": v(-451.7, 257.11) * mm, "end": v(-451.25, 258.3) * mm});
            skArc(sketch, "E237", {"start": v(-465.82, 258.07) * mm, "mid": v(-464.63, 257.41) * mm, "end": v(-463.43, 256.77) * mm});
            skArc(sketch, "E238", {"start": v(-442.67, 270.47) * mm, "mid": v(-444.33, 271.26) * mm, "end": v(-446.14, 270.9) * mm});
            skArc(sketch, "E239", {"start": v(-426.8, 387.02) * mm, "mid": v(-427.35, 385.05) * mm, "end": v(-426.69, 383.1) * mm});
            skArc(sketch, "E240", {"start": v(-398.96, 343.97) * mm, "mid": v(-397.89, 345.25) * mm, "end": v(-398.53, 346.8) * mm});
            skLineSegment(sketch, "E241", {"start": v(-469.09, 406.57) * mm, "end": v(-482.51, 403.01) * mm});
            skLineSegment(sketch, "E242", {"start": v(-486.76, 417.26) * mm, "end": v(-476.53, 419.97) * mm});
            skLineSegment(sketch, "E243", {"start": v(-399.83, 360.48) * mm, "end": v(-410.2, 361.29) * mm});
            skLineSegment(sketch, "E244", {"start": v(-400.94, 388.53) * mm, "end": v(-412.53, 387.46) * mm});
            skLineSegment(sketch, "E245", {"start": v(-566.9, 349.85) * mm, "end": v(-509.36, 387.12) * mm});
            skLineSegment(sketch, "E246", {"start": v(-561.55, 333.63) * mm, "end": v(-476.9, 393.18) * mm});
            skLineSegment(sketch, "E247", {"start": v(-529.32, 312.33) * mm, "end": v(-442.34, 363.76) * mm});
            skLineSegment(sketch, "E248", {"start": v(-577, 283.51) * mm, "end": v(-566.74, 292.74) * mm});
            skLineSegment(sketch, "E249", {"start": v(-554.23, 278.76) * mm, "end": v(-566.45, 269.88) * mm});
            skLineSegment(sketch, "E250", {"start": v(-587.57, 261.42) * mm, "end": v(-575.77, 264.61) * mm});
            skLineSegment(sketch, "E251", {"start": v(-587.76, 264.79) * mm, "end": v(-590.3, 272.9) * mm});
            skLineSegment(sketch, "E252", {"start": v(-574.04, 249.86) * mm, "end": v(-585.08, 247.63) * mm});
            skLineSegment(sketch, "E253", {"start": v(-585.08, 247.63) * mm, "end": v(-587.57, 261.42) * mm});
            skLineSegment(sketch, "E254", {"start": v(-550.48, 237.78) * mm, "end": v(-566.62, 244.08) * mm});
            skLineSegment(sketch, "E255", {"start": v(-557.82, 220.26) * mm, "end": v(-573.26, 225.35) * mm});
            skLineSegment(sketch, "E256", {"start": v(-558.54, 201.54) * mm, "end": v(-571.7, 208.27) * mm});
            skLineSegment(sketch, "E257", {"start": v(-565.58, 187.04) * mm, "end": v(-578.94, 193.02) * mm});
            skLineSegment(sketch, "E258", {"start": v(-578.94, 193.02) * mm, "end": v(-586.06, 244.8) * mm});
            skLineSegment(sketch, "E259", {"start": v(-483.5, 305.58) * mm, "end": v(-513.4, 298.75) * mm});
            skLineSegment(sketch, "E260", {"start": v(-477.74, 272.85) * mm, "end": v(-479.98, 272.85) * mm});
            skLineSegment(sketch, "E261", {"start": v(-477.74, 272.85) * mm, "end": v(-506.06, 266.38) * mm});
            skLineSegment(sketch, "E262", {"start": v(-426.21, 263.02) * mm, "end": v(-446.26, 258.04) * mm});
            skLineSegment(sketch, "E263", {"start": v(-421.56, 237.4) * mm, "end": v(-445.05, 231.63) * mm});
            skLineSegment(sketch, "E264", {"start": v(-430.91, 301.53) * mm, "end": v(-401.1, 301.53) * mm});
            skLineSegment(sketch, "E265", {"start": v(-480.27, 326.24) * mm, "end": v(-424.51, 356.36) * mm});
            skLineSegment(sketch, "E266", {"start": v(-394.6, 334.21) * mm, "end": v(-414.94, 331.36) * mm});
            skLineSegment(sketch, "E267", {"start": v(-390.76, 311.47) * mm, "end": v(-409.18, 306.7) * mm});
            skLineSegment(sketch, "E268", {"start": v(-410.65, 383.87) * mm, "end": v(-412.53, 387.46) * mm});
            skLineSegment(sketch, "E269", {"start": v(-337.87, 399.77) * mm, "end": v(-443.93, 416.76) * mm});
            skLineSegment(sketch, "E270", {"start": v(-355.15, 379.96) * mm, "end": v(-316.77, 375.41) * mm});
            skLineSegment(sketch, "E271", {"start": v(-297.8, 383.87) * mm, "end": v(-317.87, 380) * mm});
            skLineSegment(sketch, "E272", {"start": v(-300.32, 406.27) * mm, "end": v(-320.1, 403.09) * mm});
            skLineSegment(sketch, "E273", {"start": v(-320.1, 403.09) * mm, "end": v(-318.7, 399.6) * mm});
            skLineSegment(sketch, "E274", {"start": v(-318.7, 399.6) * mm, "end": v(-304.9, 401.7) * mm});
            skLineSegment(sketch, "E275", {"start": v(-320.92, 415.03) * mm, "end": v(-310.68, 416.29) * mm});
            skLineSegment(sketch, "E276", {"start": v(-475.94, 200.43) * mm, "end": v(-449.23, 209.33) * mm});
            skLineSegment(sketch, "E277", {"start": v(-439.09, 176.94) * mm, "end": v(-464.63, 169.33) * mm});
            skLineSegment(sketch, "E278", {"start": v(-464.63, 169.33) * mm, "end": v(-521.4, 212.51) * mm});
            skLineSegment(sketch, "E279", {"start": v(-537.2, 206.8) * mm, "end": v(-443.54, 131.93) * mm});
            skLineSegment(sketch, "E280", {"start": v(-531.5, 180.22) * mm, "end": v(-461.37, 119.1) * mm});
            skLineSegment(sketch, "E281", {"start": v(-541, 168.75) * mm, "end": v(-471.15, 110.18) * mm});
            skLineSegment(sketch, "E282", {"start": v(-570.39, 149.53) * mm, "end": v(-494.64, 101.49) * mm});
            skLineSegment(sketch, "E283", {"start": v(-581.12, 167.88) * mm, "end": v(-580.86, 178.5) * mm});
            skLineSegment(sketch, "E284", {"start": v(-589.43, 180.48) * mm, "end": v(-589.7, 169.3) * mm});
            skLineSegment(sketch, "E285", {"start": v(-589.7, 169.3) * mm, "end": v(-589.43, 167.34) * mm});
            skLineSegment(sketch, "E286", {"start": v(-409.47, 131.35) * mm, "end": v(-397.05, 129.97) * mm});
            skLineSegment(sketch, "E287", {"start": v(-414.13, 103.39) * mm, "end": v(-396.87, 101.84) * mm});
            skLineSegment(sketch, "E288", {"start": v(-409.3, 169.31) * mm, "end": v(-392.9, 175.18) * mm});
            skLineSegment(sketch, "E289", {"start": v(-384.97, 154.3) * mm, "end": v(-402.22, 148.78) * mm});
            skLineSegment(sketch, "E290", {"start": v(-459.88, 163.22) * mm, "end": v(-435.1, 142.4) * mm});
            skLineSegment(sketch, "E291", {"start": v(-322.17, 97.31) * mm, "end": v(-304.64, 104.99) * mm});
            skLineSegment(sketch, "E292", {"start": v(-296.4, 86.21) * mm, "end": v(-307.91, 88) * mm});
            skLineSegment(sketch, "E293", {"start": v(-309.83, 77.45) * mm, "end": v(-296.54, 83.47) * mm});
            skLineSegment(sketch, "E294", {"start": v(-336, 86.08) * mm, "end": v(-435.7, 80.6) * mm});
            skLineSegment(sketch, "E295", {"start": v(-309.7, 117.58) * mm, "end": v(-344.07, 111.96) * mm});
            skLineSegment(sketch, "E296", {"start": v(-462.31, 85.78) * mm, "end": v(-472.53, 88.6) * mm});
            skLineSegment(sketch, "E297", {"start": v(-467.32, 71.87) * mm, "end": v(-477.43, 75.34) * mm});
            skLineSegment(sketch, "E298", {"start": v(-588.63, 315.86) * mm, "end": v(-599.48, 305.16) * mm});
            skLineSegment(sketch, "E299", {"start": v(-576.12, 306.7) * mm, "end": v(-586.32, 295.48) * mm});
            skLineSegment(sketch, "E300", {"start": v(-594.4, 287.64) * mm, "end": v(-593.6, 295.65) * mm});
            skLineSegment(sketch, "E301", {"start": v(-602.55, 288.95) * mm, "end": v(-601.58, 298.72) * mm});
            skLineSegment(sketch, "E302", {"start": v(-601.58, 298.72) * mm, "end": v(-599.48, 305.16) * mm});
            skArc(sketch, "E303", {"start": v(-588.3, 294.14) * mm, "mid": v(-590.86, 295.2) * mm, "end": v(-593.6, 295.65) * mm});
            skArc(sketch, "E304", {"start": v(-588.3, 294.14) * mm, "mid": v(-587.23, 294.7) * mm, "end": v(-586.32, 295.48) * mm});
            skArc(sketch, "E305", {"start": v(-494.64, 101.49) * mm, "mid": v(-486.78, 98.34) * mm, "end": v(-478.32, 98.22) * mm});
            skArc(sketch, "E306", {"start": v(-463.43, 90.6) * mm, "mid": v(-470.09, 95.95) * mm, "end": v(-478.32, 98.22) * mm});
            skArc(sketch, "E307", {"start": v(-472.53, 88.6) * mm, "mid": v(-478.3, 83.2) * mm, "end": v(-477.43, 75.34) * mm});
            skArc(sketch, "E308", {"start": v(-462.34, 93.98) * mm, "mid": v(-465.2, 102.92) * mm, "end": v(-471.15, 110.18) * mm});
            skArc(sketch, "E309", {"start": v(-461.37, 119.1) * mm, "mid": v(-453.84, 113.8) * mm, "end": v(-445.38, 110.18) * mm});
            skArc(sketch, "E310", {"start": v(-462.31, 83.76) * mm, "mid": v(-465.9, 79.02) * mm, "end": v(-466.47, 73.1) * mm});
            skArc(sketch, "E311", {"start": v(-467.32, 71.87) * mm, "mid": v(-466.42, 72.16) * mm, "end": v(-466.47, 73.1) * mm});
            skArc(sketch, "E312", {"start": v(-462.31, 83.76) * mm, "mid": v(-462.18, 84.77) * mm, "end": v(-462.31, 85.78) * mm});
            skArc(sketch, "E313", {"start": v(-463.43, 90.6) * mm, "mid": v(-462.7, 92.23) * mm, "end": v(-462.34, 93.98) * mm});
            skArc(sketch, "E314", {"start": v(-446.76, 83.76) * mm, "mid": v(-441.5, 81.25) * mm, "end": v(-435.7, 80.6) * mm});
            skArc(sketch, "E315", {"start": v(-445.98, 85.15) * mm, "mid": v(-438.47, 97.5) * mm, "end": v(-445.38, 110.18) * mm});
            skArc(sketch, "E316", {"start": v(-445.98, 85.15) * mm, "mid": v(-446.8, 84.7) * mm, "end": v(-446.76, 83.76) * mm});
            skArc(sketch, "E317", {"start": v(-396.87, 101.84) * mm, "mid": v(-390.8, 115.94) * mm, "end": v(-397.05, 129.97) * mm});
            skArc(sketch, "E318", {"start": v(-384.97, 154.3) * mm, "mid": v(-384.6, 166.39) * mm, "end": v(-392.9, 175.18) * mm});
            skArc(sketch, "E319", {"start": v(-476.53, 419.97) * mm, "mid": v(-470.77, 415.36) * mm, "end": v(-463.43, 414.55) * mm});
            skArc(sketch, "E320", {"start": v(-462.31, 412.9) * mm, "mid": v(-465.28, 408) * mm, "end": v(-467.32, 402.63) * mm});
            skArc(sketch, "E321", {"start": v(-476.9, 393.18) * mm, "mid": v(-471.71, 397.5) * mm, "end": v(-467.32, 402.63) * mm});
            skArc(sketch, "E322", {"start": v(-462.31, 412.9) * mm, "mid": v(-462.55, 413.94) * mm, "end": v(-463.43, 414.55) * mm});
            skArc(sketch, "E323", {"start": v(-443.93, 416.76) * mm, "mid": v(-445.2, 416.06) * mm, "end": v(-444.84, 414.66) * mm});
            skArc(sketch, "E324", {"start": v(-310.37, 414.28) * mm, "mid": v(-309.55, 415.44) * mm, "end": v(-310.68, 416.29) * mm});
            skArc(sketch, "E325", {"start": v(-322.56, 405.37) * mm, "mid": v(-321.31, 404.77) * mm, "end": v(-320.3, 405.72) * mm});
            skArc(sketch, "E326", {"start": v(-316.77, 375.41) * mm, "mid": v(-315.48, 375.65) * mm, "end": v(-314.55, 376.58) * mm});
            skArc(sketch, "E327", {"start": v(-401.1, 301.53) * mm, "mid": v(-400.26, 302.1) * mm, "end": v(-400.48, 303.1) * mm});
            skArc(sketch, "E328", {"start": v(-480.27, 326.24) * mm, "mid": v(-479.04, 324.9) * mm, "end": v(-477.35, 324.27) * mm});
            skArc(sketch, "E329", {"start": v(-445.05, 231.63) * mm, "mid": v(-446.8, 229.58) * mm, "end": v(-445.4, 227.27) * mm});
            skArc(sketch, "E330", {"start": v(-510.63, 306.79) * mm, "mid": v(-513, 303.11) * mm, "end": v(-513.4, 298.75) * mm});
            skArc(sketch, "E331", {"start": v(-510.63, 306.79) * mm, "mid": v(-512.02, 307.04) * mm, "end": v(-513.4, 306.79) * mm});
            skLineSegment(sketch, "E332", {"start": v(-525.18, 299.5) * mm, "end": v(-513.4, 306.79) * mm});
            skLineSegment(sketch, "E333", {"start": v(-546.2, 262.2) * mm, "end": v(-499.35, 258.72) * mm});
            skArc(sketch, "E334", {"start": v(-506.06, 266.38) * mm, "mid": v(-503.18, 262.13) * mm, "end": v(-499.35, 258.72) * mm});
            skArc(sketch, "E335", {"start": v(-442.3, 239.45) * mm, "mid": v(-438.5, 236.81) * mm, "end": v(-433.98, 235.84) * mm});
            skArc(sketch, "E336", {"start": v(-442.3, 239.45) * mm, "mid": v(-450.75, 242.07) * mm, "end": v(-459.49, 243.49) * mm});
            skArc(sketch, "E337", {"start": v(-434.53, 234.22) * mm, "mid": v(-434.16, 235) * mm, "end": v(-433.98, 235.84) * mm});
            skArc(sketch, "E338", {"start": v(-425.85, 239.45) * mm, "mid": v(-422.93, 250.74) * mm, "end": v(-432.48, 257.45) * mm});
            skArc(sketch, "E339", {"start": v(-432.48, 257.45) * mm, "mid": v(-437.46, 257.12) * mm, "end": v(-442.3, 255.93) * mm});
            skArc(sketch, "E340", {"start": v(-450.15, 255.38) * mm, "mid": v(-446.22, 255.56) * mm, "end": v(-442.3, 255.93) * mm});
            skArc(sketch, "E341", {"start": v(-427.3, 236) * mm, "mid": v(-426.5, 237.7) * mm, "end": v(-425.85, 239.45) * mm});
            skLineSegment(sketch, "E342", {"start": v(-547.98, 249.86) * mm, "end": v(-459.49, 243.49) * mm});
            skLineSegment(sketch, "E343", {"start": v(-446.26, 258.04) * mm, "end": v(-451.25, 258.3) * mm});
            skLineSegment(sketch, "E344", {"start": v(-452.78, 256.44) * mm, "end": v(-450.15, 255.38) * mm});
            skLineSegment(sketch, "E345", {"start": v(-584.4, 245.54) * mm, "end": v(-586.06, 244.8) * mm});
            skArc(sketch, "E346", {"start": v(-414.13, 103.39) * mm, "mid": v(-405.38, 116.3) * mm, "end": v(-409.47, 131.35) * mm});
            skArc(sketch, "E347", {"start": v(-430.92, 118.77) * mm, "mid": v(-427.95, 109.29) * mm, "end": v(-419.96, 103.39) * mm});
            skArc(sketch, "E348", {"start": v(-430.92, 118.77) * mm, "mid": v(-436.8, 125.76) * mm, "end": v(-443.54, 131.93) * mm});
            skArc(sketch, "E349", {"start": v(-419.96, 103.39) * mm, "mid": v(-408.62, 92.5) * mm, "end": v(-393.52, 88.09) * mm});
            skArc(sketch, "E350", {"start": v(-393.52, 88.09) * mm, "mid": v(-382.58, 91.03) * mm, "end": v(-373.93, 98.36) * mm});
            skArc(sketch, "E351", {"start": v(-344.07, 111.96) * mm, "mid": v(-359.91, 107.16) * mm, "end": v(-373.93, 98.36) * mm});
            skArc(sketch, "E352", {"start": v(-435.1, 142.4) * mm, "mid": v(-426.5, 136.78) * mm, "end": v(-416.83, 133.36) * mm});
            skArc(sketch, "E353", {"start": v(-399.57, 142.4) * mm, "mid": v(-408.88, 139.18) * mm, "end": v(-416.83, 133.36) * mm});
            skArc(sketch, "E354", {"start": v(-402.22, 148.78) * mm, "mid": v(-400.47, 145.9) * mm, "end": v(-397.65, 144.04) * mm});
            skArc(sketch, "E355", {"start": v(-399.57, 142.4) * mm, "mid": v(-398.43, 143.01) * mm, "end": v(-397.65, 144.04) * mm});
            skArc(sketch, "E356", {"start": v(-458.42, 165.32) * mm, "mid": v(-444.79, 162.76) * mm, "end": v(-431.3, 166) * mm});
            skArc(sketch, "E357", {"start": v(-431.3, 166) * mm, "mid": v(-422.66, 171.16) * mm, "end": v(-417.33, 179.7) * mm});
            skArc(sketch, "E358", {"start": v(-401.3, 188.06) * mm, "mid": v(-409.96, 185.1) * mm, "end": v(-417.33, 179.7) * mm});
            skArc(sketch, "E359", {"start": v(-401.3, 188.06) * mm, "mid": v(-397.4, 187.92) * mm, "end": v(-393.5, 188.06) * mm});
            skArc(sketch, "E360", {"start": v(-395.55, 186.69) * mm, "mid": v(-404.03, 179.27) * mm, "end": v(-409.3, 169.31) * mm});
            skArc(sketch, "E361", {"start": v(-395.55, 186.69) * mm, "mid": v(-394.45, 187.26) * mm, "end": v(-393.5, 188.06) * mm});
            skArc(sketch, "E362", {"start": v(-458.42, 165.32) * mm, "mid": v(-459.53, 164.53) * mm, "end": v(-459.88, 163.22) * mm});
            skArc(sketch, "E363", {"start": v(-457.22, 388.86) * mm, "mid": v(-452.26, 389.36) * mm, "end": v(-447.58, 391.1) * mm});
            skArc(sketch, "E364", {"start": v(-457.22, 388.86) * mm, "mid": v(-461.9, 386.55) * mm, "end": v(-466.24, 383.64) * mm});
            skLineSegment(sketch, "E365", {"start": v(-466.24, 383.64) * mm, "end": v(-555.87, 321.7) * mm});
            skArc(sketch, "E366", {"start": v(-336, 86.08) * mm, "mid": v(-325.95, 88.52) * mm, "end": v(-317.46, 94.42) * mm});
            skArc(sketch, "E367", {"start": v(-301.58, 94.42) * mm, "mid": v(-309.52, 96.9) * mm, "end": v(-317.46, 94.42) * mm});
            skArc(sketch, "E368", {"start": v(-295.88, 88.9) * mm, "mid": v(-298.7, 91.7) * mm, "end": v(-301.58, 94.42) * mm});
            skArc(sketch, "E369", {"start": v(-293.99, 88.9) * mm, "mid": v(-297.15, 98.37) * mm, "end": v(-304.64, 104.99) * mm});
            skArc(sketch, "E370", {"start": v(-307.91, 88) * mm, "mid": v(-310.05, 82.94) * mm, "end": v(-309.83, 77.45) * mm});
            skArc(sketch, "E371", {"start": v(-309.7, 115.52) * mm, "mid": v(-317.5, 107.5) * mm, "end": v(-322.17, 97.31) * mm});
            skLineSegment(sketch, "E372", {"start": v(-309.7, 115.52) * mm, "end": v(-309.7, 117.58) * mm});
            skLineSegment(sketch, "E373", {"start": v(-295.88, 88.9) * mm, "end": v(-293.99, 88.9) * mm});
            skLineSegment(sketch, "E374", {"start": v(-296.4, 86.21) * mm, "end": v(-296.54, 83.47) * mm});
            skCircle(sketch, "E375.cCircle", {"center": v(-454.05, 402.3) * mm, "radius": 7.94 * mm, "construction": true});
            skLineSegment(sketch, "E375.0", {"start": v(-444.9, 401.95) * mm, "end": v(-449.78, 394.2) * mm});
            skLineSegment(sketch, "E375.1", {"start": v(-449.78, 394.2) * mm, "end": v(-458.94, 394.54) * mm});
            skLineSegment(sketch, "E375.2", {"start": v(-458.94, 394.54) * mm, "end": v(-463.21, 402.65) * mm});
            skLineSegment(sketch, "E375.3", {"start": v(-463.21, 402.65) * mm, "end": v(-458.33, 410.4) * mm});
            skLineSegment(sketch, "E375.4", {"start": v(-458.33, 410.4) * mm, "end": v(-449.17, 410.05) * mm});
            skLineSegment(sketch, "E375.5", {"start": v(-449.17, 410.05) * mm, "end": v(-444.9, 401.95) * mm});
            skPoint(sketch, "E375.0.midPoint", {"position": v(-447.34, 398.07) * mm});
            skCircle(sketch, "E376.cCircle", {"center": v(-465.39, 426.65) * mm, "radius": 7.94 * mm, "construction": true});
            skLineSegment(sketch, "E376.0", {"start": v(-473.32, 422.07) * mm, "end": v(-473.32, 431.23) * mm});
            skLineSegment(sketch, "E376.1", {"start": v(-473.32, 431.23) * mm, "end": v(-465.39, 435.81) * mm});
            skLineSegment(sketch, "E376.2", {"start": v(-465.39, 435.81) * mm, "end": v(-457.45, 431.23) * mm});
            skLineSegment(sketch, "E376.3", {"start": v(-457.45, 431.23) * mm, "end": v(-457.45, 422.07) * mm});
            skLineSegment(sketch, "E376.4", {"start": v(-457.45, 422.07) * mm, "end": v(-465.39, 417.48) * mm});
            skLineSegment(sketch, "E376.5", {"start": v(-465.39, 417.48) * mm, "end": v(-473.32, 422.07) * mm});
            skPoint(sketch, "E376.0.midPoint", {"position": v(-473.32, 426.65) * mm});
            skCircle(sketch, "E377.cCircle", {"center": v(-594.4, 338.29) * mm, "radius": 7.14 * mm, "construction": true});
            skLineSegment(sketch, "E377.0", {"start": v(-588.53, 332.5) * mm, "end": v(-596.47, 330.31) * mm});
            skLineSegment(sketch, "E377.1", {"start": v(-596.47, 330.31) * mm, "end": v(-602.34, 336.1) * mm});
            skLineSegment(sketch, "E377.2", {"start": v(-602.34, 336.1) * mm, "end": v(-600.26, 344.08) * mm});
            skLineSegment(sketch, "E377.3", {"start": v(-600.26, 344.08) * mm, "end": v(-592.31, 346.26) * mm});
            skLineSegment(sketch, "E377.4", {"start": v(-592.31, 346.26) * mm, "end": v(-586.45, 340.47) * mm});
            skLineSegment(sketch, "E377.5", {"start": v(-586.45, 340.47) * mm, "end": v(-588.53, 332.5) * mm});
            skPoint(sketch, "E377.0.midPoint", {"position": v(-592.5, 331.4) * mm});
            skCircle(sketch, "E378.cCircle", {"center": v(-595.96, 158.13) * mm, "radius": 7.14 * mm, "construction": true});
            skLineSegment(sketch, "E378.0", {"start": v(-598.38, 150.25) * mm, "end": v(-604, 156.28) * mm});
            skLineSegment(sketch, "E378.1", {"start": v(-604, 156.28) * mm, "end": v(-601.58, 164.16) * mm});
            skLineSegment(sketch, "E378.2", {"start": v(-601.58, 164.16) * mm, "end": v(-593.55, 166) * mm});
            skLineSegment(sketch, "E378.3", {"start": v(-593.55, 166) * mm, "end": v(-587.93, 159.98) * mm});
            skLineSegment(sketch, "E378.4", {"start": v(-587.93, 159.98) * mm, "end": v(-590.35, 152.1) * mm});
            skLineSegment(sketch, "E378.5", {"start": v(-590.35, 152.1) * mm, "end": v(-598.38, 150.25) * mm});
            skPoint(sketch, "E378.0.midPoint", {"position": v(-601.19, 153.27) * mm});
            skCircle(sketch, "E379.cCircle", {"center": v(-450.47, 97.79) * mm, "radius": 7.94 * mm, "construction": true});
            skLineSegment(sketch, "E379.0", {"start": v(-454.66, 89.64) * mm, "end": v(-459.62, 97.34) * mm});
            skLineSegment(sketch, "E379.1", {"start": v(-459.62, 97.34) * mm, "end": v(-455.44, 105.5) * mm});
            skLineSegment(sketch, "E379.2", {"start": v(-455.44, 105.5) * mm, "end": v(-446.29, 105.94) * mm});
            skLineSegment(sketch, "E379.3", {"start": v(-446.29, 105.94) * mm, "end": v(-441.32, 98.24) * mm});
            skLineSegment(sketch, "E379.4", {"start": v(-441.32, 98.24) * mm, "end": v(-445.5, 90.09) * mm});
            skLineSegment(sketch, "E379.5", {"start": v(-445.5, 90.09) * mm, "end": v(-454.66, 89.64) * mm});
            skPoint(sketch, "E379.0.midPoint", {"position": v(-457.14, 93.49) * mm});
            skCircle(sketch, "E380.cCircle", {"center": v(-454.79, 73.46) * mm, "radius": 7.14 * mm, "construction": true});
            skLineSegment(sketch, "E380.0", {"start": v(-456.4, 65.38) * mm, "end": v(-462.6, 70.82) * mm});
            skLineSegment(sketch, "E380.1", {"start": v(-462.6, 70.82) * mm, "end": v(-460.97, 78.9) * mm});
            skLineSegment(sketch, "E380.2", {"start": v(-460.97, 78.9) * mm, "end": v(-453.16, 81.54) * mm});
            skLineSegment(sketch, "E380.3", {"start": v(-453.16, 81.54) * mm, "end": v(-446.98, 76.1) * mm});
            skLineSegment(sketch, "E380.4", {"start": v(-446.98, 76.1) * mm, "end": v(-448.6, 68.01) * mm});
            skLineSegment(sketch, "E380.5", {"start": v(-448.6, 68.01) * mm, "end": v(-456.4, 65.38) * mm});
            skPoint(sketch, "E380.0.midPoint", {"position": v(-459.5, 68.1) * mm});
            skCircle(sketch, "E381.cCircle", {"center": v(-418.54, 118.67) * mm, "radius": 8.73 * mm, "construction": true});
            skLineSegment(sketch, "E381.0", {"start": v(-424.1, 110.26) * mm, "end": v(-428.6, 119.28) * mm});
            skLineSegment(sketch, "E381.1", {"start": v(-428.6, 119.28) * mm, "end": v(-423.05, 127.69) * mm});
            skLineSegment(sketch, "E381.2", {"start": v(-423.05, 127.69) * mm, "end": v(-412.99, 127.08) * mm});
            skLineSegment(sketch, "E381.3", {"start": v(-412.99, 127.08) * mm, "end": v(-408.48, 118.07) * mm});
            skLineSegment(sketch, "E381.4", {"start": v(-408.48, 118.07) * mm, "end": v(-414.03, 109.65) * mm});
            skLineSegment(sketch, "E381.5", {"start": v(-414.03, 109.65) * mm, "end": v(-424.1, 110.26) * mm});
            skPoint(sketch, "E381.0.midPoint", {"position": v(-426.35, 114.77) * mm});
            skCircle(sketch, "E382.cCircle", {"center": v(-433.81, 246.66) * mm, "radius": 7.14 * mm, "construction": true});
            skLineSegment(sketch, "E382.0", {"start": v(-433.25, 238.44) * mm, "end": v(-440.65, 242.07) * mm});
            skLineSegment(sketch, "E382.1", {"start": v(-440.65, 242.07) * mm, "end": v(-441.22, 250.29) * mm});
            skLineSegment(sketch, "E382.2", {"start": v(-441.22, 250.29) * mm, "end": v(-434.38, 254.89) * mm});
            skLineSegment(sketch, "E382.3", {"start": v(-434.38, 254.89) * mm, "end": v(-426.97, 251.26) * mm});
            skLineSegment(sketch, "E382.4", {"start": v(-426.97, 251.26) * mm, "end": v(-426.41, 243.04) * mm});
            skLineSegment(sketch, "E382.5", {"start": v(-426.41, 243.04) * mm, "end": v(-433.25, 238.44) * mm});
            skPoint(sketch, "E382.0.midPoint", {"position": v(-436.95, 240.25) * mm});
            skCircle(sketch, "E383.cCircle", {"center": v(-417.84, 373.73) * mm, "radius": 8.74 * mm, "construction": true});
            skLineSegment(sketch, "E383.0", {"start": v(-407.78, 372.92) * mm, "end": v(-413.51, 364.62) * mm});
            skLineSegment(sketch, "E383.1", {"start": v(-413.51, 364.62) * mm, "end": v(-423.57, 365.43) * mm});
            skLineSegment(sketch, "E383.2", {"start": v(-423.57, 365.43) * mm, "end": v(-427.9, 374.55) * mm});
            skLineSegment(sketch, "E383.3", {"start": v(-427.9, 374.55) * mm, "end": v(-422.16, 382.85) * mm});
            skLineSegment(sketch, "E383.4", {"start": v(-422.16, 382.85) * mm, "end": v(-412.1, 382.04) * mm});
            skLineSegment(sketch, "E383.5", {"start": v(-412.1, 382.04) * mm, "end": v(-407.78, 372.92) * mm});
            skPoint(sketch, "E383.0.midPoint", {"position": v(-410.65, 368.77) * mm});
            skSolve(sketch);
        }
        {
            var Q0;
            Q0=makeQuery(id+"F0.imprint","IMPRINT",FACE,{"disambiguationData":[TD([[makeQuery(id+"F0.imprint","IMPRINT",EDGE,{"derivedFrom":sQuery(id+"F0.wireOp",EDGE,"E0")}),1.0]])]});
            extrude(context, id + "F1", {"entities" : qUnion([Q0]), "depth" : 6.35 * mm, "offsetDistance" : 25.4 * mm});
        }
    });
